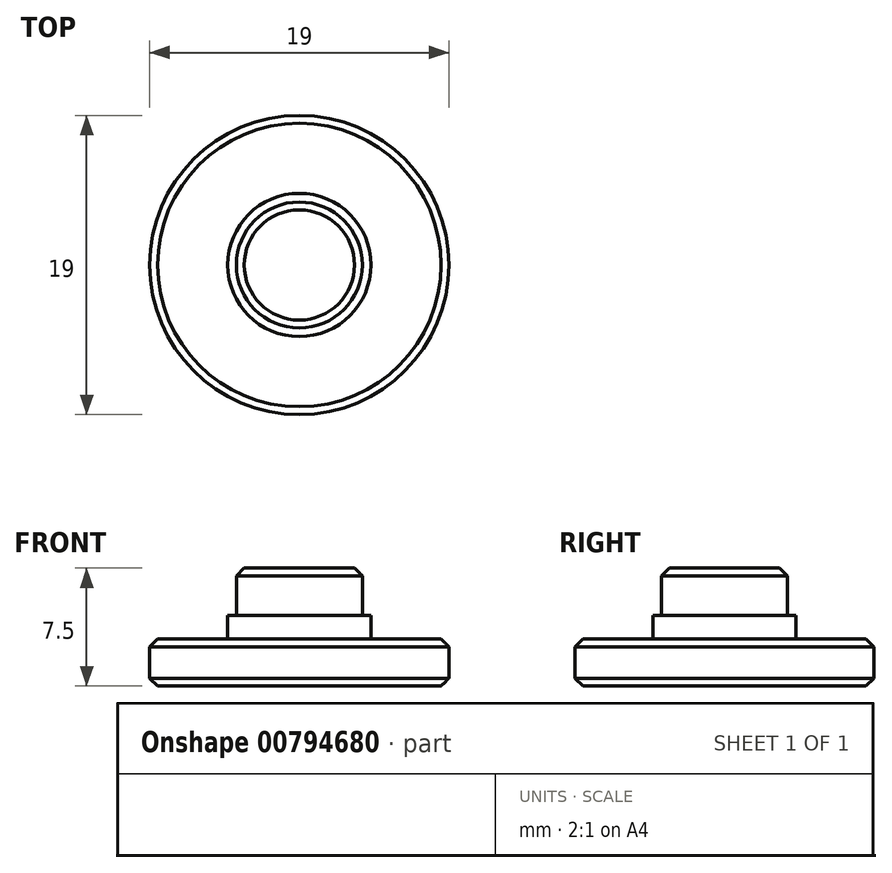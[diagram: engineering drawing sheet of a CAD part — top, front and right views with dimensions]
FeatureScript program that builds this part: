
annotation { "Feature Type Name" : "Feature", "Feature Type Description" : "" }
export const myFeature = defineFeature(function(context is Context, id is Id, definition is map)
    precondition{}
    {
        {
            var Q0;
            Q0=qCreatedBy(makeId("Top.planeOp"),FACE);
            var sketch = newSketch(context, id + "F0", { "sketchPlane" : qUnion([Q0])});
            skCircle(sketch, "E0", {"center": v(0, 0) * mm, "radius": 9.5 * mm});
            skSolve(sketch);
        }
        {
            var Q0;
            Q0 = qSketchRegion(id + "F0", true);
            extrude(context, id + "F1", {"entities" : qUnion([Q0]), "depth" : 3 * mm, "offsetDistance" : 25 * mm});
        }
        {
            var Q0;
            Q0=makeQuery(id+"F1.opExtrude","CAP_FACE",FACE,{"disambiguationData":[OSD([sQuery(id+"F0.wireOp",EDGE,"E0")])],"isStart":false});
            var sketch = newSketch(context, id + "F2", { "sketchPlane" : qUnion([Q0])});
            skCircle(sketch, "E1", {"center": v(0, 0) * mm, "radius": 4 * mm});
            skSolve(sketch);
        }
        {
            var Q0;
            Q0 = qSketchRegion(id + "F2", true);
            extrude(context, id + "F3", {"entities" : qUnion([Q0]), "operationType" : NewBodyOperationType.ADD, "depth" : 4.5 * mm, "offsetDistance" : 25 * mm});
        }
        {
            var Q0;
            Q0=makeQuery(id+"F3.opExtrude","CAP_EDGE",EDGE,{"disambiguationData":[OSD([sQuery(id+"F2.wireOp",EDGE,"E1")])],"isStart":false});
            var Q1;
            Q1=makeQuery(id+"F1.opExtrude","CAP_EDGE",EDGE,{"disambiguationData":[OSD([sQuery(id+"F0.wireOp",EDGE,"E0")])],"isStart":false});
            var Q2;
            Q2=makeQuery(id+"F1.opExtrude","CAP_EDGE",EDGE,{"disambiguationData":[OSD([sQuery(id+"F0.wireOp",EDGE,"E0")])],"isStart":true});
            chamfer(context, id + "F4", {"entities" : qUnion([Q0, Q1, Q2]), "width" : 0.5 * mm, "tangentPropagation" : true});
        }
        {
            var Q0;
            Q0=makeQuery(id+"F1.opExtrude","CAP_FACE",FACE,{"disambiguationData":[OSD([sQuery(id+"F0.wireOp",EDGE,"E0")])],"isStart":false});
            var sketch = newSketch(context, id + "F5", { "sketchPlane" : qUnion([Q0])});
            skCircle(sketch, "E2", {"center": v(0, 0) * mm, "radius": 4.55 * mm});
            skSolve(sketch);
        }
        {
            var Q0;
            Q0 = qSketchRegion(id + "F5", true);
            extrude(context, id + "F6", {"entities" : qUnion([Q0]), "operationType" : NewBodyOperationType.ADD, "depth" : 1.5 * mm, "offsetDistance" : 25 * mm});
        }
    });
